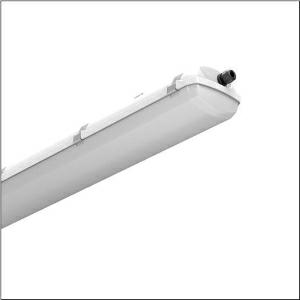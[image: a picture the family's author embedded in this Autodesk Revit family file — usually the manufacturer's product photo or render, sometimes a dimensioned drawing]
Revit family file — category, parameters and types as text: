
# Revit family: monsun_ex_51fxa27l460a
name_source: partatom
category: Lighting Fixtures
units: mm (PartAtom-declared; Revit-internal decimal feet)

## family parameters
Cut with Voids When Loaded = No
Host = Face
Light Source = No
Part Type = Normal
Room Calculation Point = No
Round Connector Dimension = Use Diameter
Shared = No

## types (1)
- Monsun Ex (1 x LED, 6560 lm, 53 W, 4000K)
    Apparent Load = 53 VA
    CIE Flux Codes = 46 76 94 98 100
    Color Rendering = 80
    Color Temperature = 4000K
    Default Elevation = 1800 mm
    Description = Monsun Ex, damp-proof luminaire, primary optical cover: cover, of PC, UV-stabilised, opal, light emission: direct distribution, primary light characteristic: symmetric, installation type: surface-mounted, LED, rated luminous flux: 6.560lm, luminous efficacy: 124lm/W, light colour: 840, colour temperature: 4000K, control gear: ON/OFF, with terminal, 3-pole, max. 2.5mm², through-wiring: 5x 2.5mm², mains connection: 220..250V, AC, 50/60Hz, rated input power: 53W, housing, of PC, light grey (RAL 7035), incl. 2x Ex cable gland M20 for cable diameter 7..12mm with sealing, incl. 1x Ex locking screw M20 with sealing, length: 1.280mm, width: 155mm, height: 105mm, clip for enclosure, of stainless steel, protection rating (complete): IP66, insulation class (complete): insulation class I (protective earthing), certification: CE, explosion class: zone 1,21 II 2G Ex eb mb op is IIC T4 Gb, II 2D Ex tb op is IIIC T67°C Db, impact resistance: IK10, permissible operating ambient temperature: -20..+40°C, contact your sales advisor before using the luminaires in applications with unclear chemical exposure, large temperature fluctuations or condensation-forming humidity, packaging unit: 1 piece
    Height = 105 mm
    Lamp = 1 x LED
    Lamp Light Flux = 6560 lm
    Lamp Power = 53 W
    Lamp count = 1
    Length = 1280 mm
    Luminous efficacy = 124 lm/W
    Manufacturer = Siteco
    ModVariant = No
    Model = 51FXA27L460A
    Mounting Place = Ceiling
    Mounting Type = Surface mounted
    Number of Poles = 1
    OnlyDefault = Yes
    Power Factor = 1
    Product Name = Monsun Ex
    Product group = damp-proof luminaire
    ProductGroupID = 300
    Protection Class = Protection class I
    Protection Degree = IP 66
    RLX_Detail_Level = 1
    RLX_Emergency_Light_Flux = 0 lm
    RLX_Emergency_Type = 0
    RLX_Emergency_Type_DB = No
    RlxData = <blob elided: 41601 chars, md5=8ae49fc6>
    Socket = socket
    Standby Power = 0 W
    System Light Flux = 6560 lm
    System Power = 53 W
    Type Comments = Product without accessories
    Type Image = l_1258882.jpg
    URL = http://relux.com
    VarID = ---
    Voltage = 0 V
    Weight = 0.00 kg
    Width = 155 mm

## geometry (parser evidence)
native form markers: Blend x4, Sweep x10
no freeform markers — native parametric forms only
